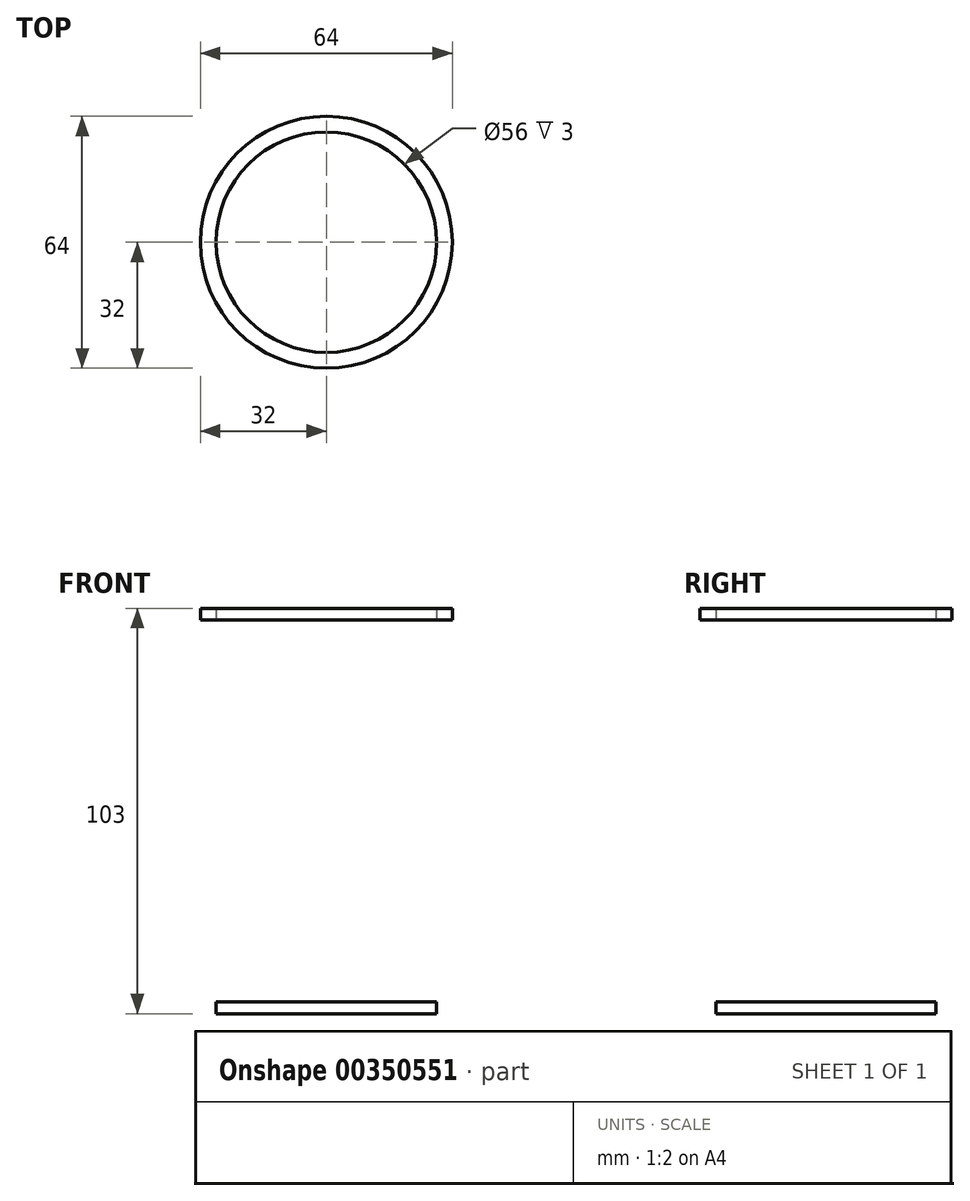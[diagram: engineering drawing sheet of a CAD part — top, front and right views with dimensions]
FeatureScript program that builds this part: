
annotation { "Feature Type Name" : "Feature", "Feature Type Description" : "" }
export const myFeature = defineFeature(function(context is Context, id is Id, definition is map)
    precondition{}
    {
        {
            var Q0;
            Q0=qCreatedBy(makeId("Front.planeOp"),FACE);
            var sketch = newSketch(context, id + "F0", { "sketchPlane" : qUnion([Q0])});
            skLineSegment(sketch, "E0.bottom", {"start": v(0, 0) * mm, "end": v(28, 0) * mm});
            skLineSegment(sketch, "E0.top", {"start": v(0, 3) * mm, "end": v(28, 3) * mm});
            skLineSegment(sketch, "E0.left", {"start": v(0, 0) * mm, "end": v(0, 3) * mm});
            skLineSegment(sketch, "E0.right", {"start": v(28, 0) * mm, "end": v(28, 3) * mm});
            skLineSegment(sketch, "E1.bottom", {"start": v(0, 3) * mm, "end": v(3, 3) * mm});
            skLineSegment(sketch, "E1.top", {"start": v(0, 103) * mm, "end": v(3, 103) * mm});
            skLineSegment(sketch, "E1.left", {"start": v(0, 3) * mm, "end": v(0, 103) * mm});
            skLineSegment(sketch, "E1.right", {"start": v(3, 3) * mm, "end": v(3, 103) * mm});
            skLineSegment(sketch, "E2.bottom", {"start": v(-4, 103) * mm, "end": v(0, 103) * mm});
            skLineSegment(sketch, "E2.top", {"start": v(-4, 100) * mm, "end": v(0, 100) * mm});
            skLineSegment(sketch, "E2.left", {"start": v(-4, 103) * mm, "end": v(-4, 100) * mm});
            skLineSegment(sketch, "E2.right", {"start": v(0, 103) * mm, "end": v(0, 100) * mm});
            skSolve(sketch);
        }
        {
            var Q0;
            Q0=makeQuery(id+"F0.imprint","IMPRINT",FACE,{"disambiguationData":[TD([[makeQuery(id+"F0.imprint","IMPRINT",EDGE,{"derivedFrom":sQuery(id+"F0.wireOp",EDGE,"E0.bottom")}),1.0]])]});
            var Q1;
            Q1=makeQuery(id+"F0.imprint","IMPRINT",FACE,{"disambiguationData":[TD([[makeQuery(id+"F0.imprint","IMPRINT",EDGE,{"derivedFrom":sQuery(id+"F0.wireOp",EDGE,"E1.bottom")}),1.0]])]});
            var Q2;
            Q2=makeQuery(id+"F0.imprint","IMPRINT",FACE,{"disambiguationData":[TD([[makeQuery(id+"F0.imprint","IMPRINT",EDGE,{"derivedFrom":sQuery(id+"F0.wireOp",EDGE,"E2.bottom")}),-1.0]])]});
            var Q3;
            Q3=sQuery(id+"F0.wireOp",EDGE,"E0.right");
            revolve(context, id + "F1", {"entities" : qUnion([Q0, Q1, Q2]), "axis" : qUnion([Q3]), "revolveType" : RevolveType.FULL});
        }
    });
